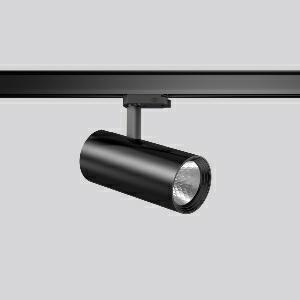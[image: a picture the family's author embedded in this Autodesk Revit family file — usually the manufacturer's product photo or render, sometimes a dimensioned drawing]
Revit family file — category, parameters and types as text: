
# Revit family: deecos_s_mini_742204_003_2_76_ed70
name_source: partatom
category: Lighting Fixtures
units: mm (PartAtom-declared; Revit-internal decimal feet)

## family parameters
Cut with Voids When Loaded = No
Host = Face
Light Source = No
Part Type = Normal
Room Calculation Point = No
Round Connector Dimension = Use Diameter
Shared = No

## types (1)
- DEECOS S mini (1 x LED Modul 927, 3300 lm, 2700)
    Apparent Load = 29 VA
    Approval mark = CE
    CIE Flux Codes = 99 100 100 100 100
    Color Rendering = 92
    Color Temperature = 2700
    Default Elevation = 1800 mm
    Description = Series: DEECOS S mini
LED surface-mounted projector in modern design with no visible cooling ribs. Housing: die-cast aluminium, powder-coated. Rotation range: 356°. Swivel range: 90°. Black plastic ring and recessed LED to prevent glare from the side. Optical assembly with reflector made of MIRO-Silver with 98% total light reflection for outstanding efficiency - can be changed without tools. Best colour rendering index Ra>90. With adapter for RZB 3-circuit DALI tracks. Suitable for Track on ceiling, Wall track. High quality converter without flickering and stroboscopic effect. The following accessories can be mounted without use of tools: interchangeable lenses, decorative glasses, honeycomb louvre, clear and frosted diffusers, white interchangeable plastic ring. 
Colour: deep black, matt (RAL 9005)
Diameter: 87 mm
Height: 214 mm
Lamp: LED
Socket: without socket
Colour temperature: 2700K
Colour rendering index (CRI): 92
System power: 29 W
Rated luminous flux: 3300 lm
Luminous efficiency: 114 lm/W
Control gear: Converter, dimmable, DALI
Protection class: I
Type of protection: IP 20
    Height = 214 mm
    Lamp = 1 x LED Modul 927
    Lamp Light Flux = 3300 lm
    Lamp count = 1
    Length = 87 mm
    Lifetime = 50000 h
    Luminous efficacy = 114 lm/W
    Manufacturer = RZB
    ModVariant = No
    Model = 742204.003.2.76
    Mounting Place = Ceiling
    Mounting Type = Rail mounted
    Number of Poles = 1
    OnlyDefault = Yes
    Power Factor = 1
    Product Name = DEECOS S mini
    Product group = Track mounted projectors
    ProductGroupID = 301
    Protection Class = Protection class I
    Protection Degree = IP 20
    RLX_Detail_Level = 1
    RLX_Emergency_Light_Flux = 0 lm
    RLX_Emergency_Type = 0
    RLX_Emergency_Type_DB = No
    RlxData = <blob elided: 38625 chars, md5=1366e029>
    Socket = socket
    Standby Power = 0 W
    System Light Flux = 3300 lm
    System Power = 29 W
    Type Comments = Product without accessories
    Type Image = 741926.003.jpg
    URL = http://relux.com
    VarID = ---
    Voltage = 230 V
    Voltage Range = 220-240 V
    Weight = 0.00 kg
    Width = 0 mm  [stored 0 ft]

note: [stored X ft] marks values corroborated as IEEE doubles in the binary element streams (Revit-internal decimal feet)

## geometry (parser evidence)
native form markers: Blend x4, Sweep x12
no freeform markers — native parametric forms only
